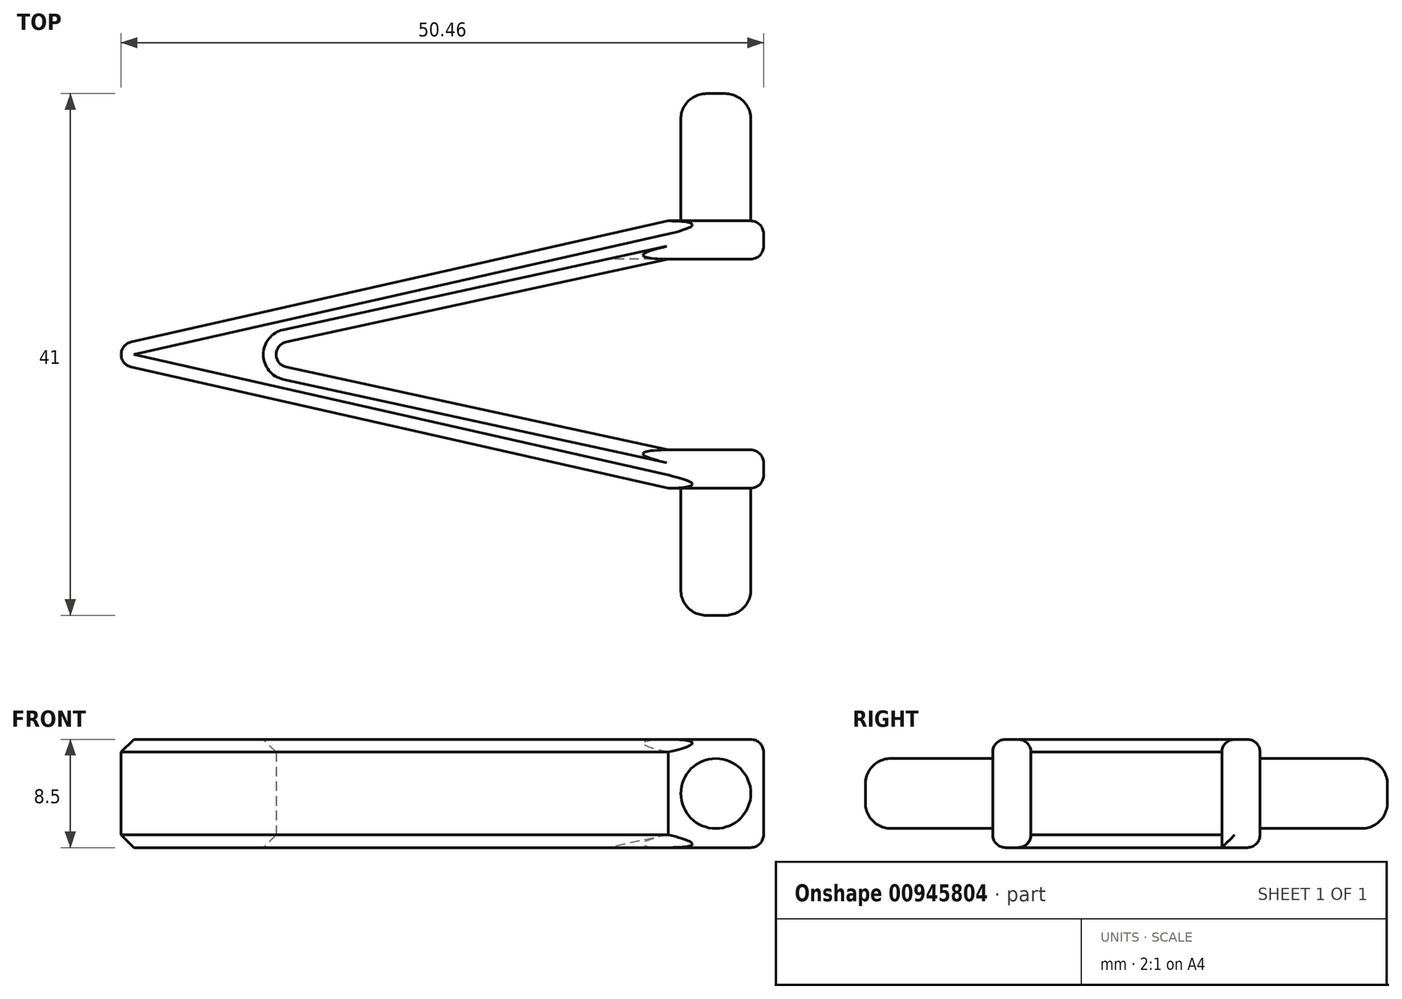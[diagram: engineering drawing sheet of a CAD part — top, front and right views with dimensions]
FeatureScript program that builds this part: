
annotation { "Feature Type Name" : "Feature", "Feature Type Description" : "" }
export const myFeature = defineFeature(function(context is Context, id is Id, definition is map)
    precondition{}
    {
        {
            var Q0;
            Q0=qCreatedBy(makeId("Top.planeOp"),FACE);
            var sketch = newSketch(context, id + "F0", { "sketchPlane" : qUnion([Q0])});
            skLineSegment(sketch, "E0", {"start": v(0, 10.5) * mm, "end": v(0, -10.5) * mm, "construction": true});
            skLineSegment(sketch, "E1", {"start": v(0, 0) * mm, "end": v(-54, 0) * mm, "construction": true});
            skPoint(sketch, "E1.endSnap0", {"position": v(0, 0) * mm});
            skLineSegment(sketch, "E2", {"start": v(0, 10.5) * mm, "end": v(-7.5, 10.5) * mm});
            skLineSegment(sketch, "E3", {"start": v(-7.5, 10.5) * mm, "end": v(-54, 0) * mm});
            skLineSegment(sketch, "E4", {"start": v(0, 10.5) * mm, "end": v(0, 7.5) * mm});
            skLineSegment(sketch, "E5", {"start": v(0, 7.5) * mm, "end": v(-7.5, 7.5) * mm});
            skLineSegment(sketch, "E6", {"start": v(-7.5, 7.5) * mm, "end": v(-42, 0) * mm});
            skLineSegment(sketch, "E7.MirrorCS", {"start": v(-7.5, -10.5) * mm, "end": v(-54, 0) * mm});
            skLineSegment(sketch, "E8.MirrorCS", {"start": v(0, -7.5) * mm, "end": v(-7.5, -7.5) * mm});
            skLineSegment(sketch, "E9.MirrorCS", {"start": v(0, -10.5) * mm, "end": v(0, -7.5) * mm});
            skLineSegment(sketch, "E10.MirrorCS", {"start": v(0, -10.5) * mm, "end": v(-7.5, -10.5) * mm});
            skLineSegment(sketch, "E11.MirrorCS", {"start": v(-7.5, -7.5) * mm, "end": v(-42, 0) * mm});
            skSolve(sketch);
        }
        {
            var Q0;
            Q0 = qSketchRegion(id + "F0", true);
            extrude(context, id + "F1", {"entities" : qUnion([Q0]), "depth" : 8.5 * mm, "offsetDistance" : 25 * mm});
        }
        {
            var Q0;
            Q0=makeQuery(id+"F1.opExtrude","SWEPT_EDGE",EDGE,{"disambiguationData":[OSD([sQuery(id+"F0.wireOp",EDGE,"E6"),sQuery(id+"F0.wireOp",EDGE,"E11.MirrorCS")])]});
            fillet(context, id + "F2", {"entities" : qUnion([Q0]), "radius" : 1 * mm, "tangentPropagation" : true, "allowEdgeOverflow" : false});
        }
        {
            var Q0;
            Q0=makeQuery(id+"F1.opExtrude","SWEPT_EDGE",EDGE,{"disambiguationData":[OSD([sQuery(id+"F0.wireOp",EDGE,"E3"),sQuery(id+"F0.wireOp",EDGE,"E7.MirrorCS")])]});
            fillet(context, id + "F3", {"entities" : qUnion([Q0]), "radius" : 1 * mm, "tangentPropagation" : true, "allowEdgeOverflow" : false});
        }
        {
            var Q0;
            Q0=makeQuery(id+"F1.opExtrude","SWEPT_FACE",FACE,{"disambiguationData":[OSD([sQuery(id+"F0.wireOp",EDGE,"E2")])]});
            var sketch = newSketch(context, id + "F4", { "sketchPlane" : qUnion([Q0])});
            skCircle(sketch, "E12", {"center": v(3.75, 4.25) * mm, "radius": 2.75 * mm});
            skLineSegment(sketch, "E13", {"start": v(7.5, 8.5) * mm, "end": v(0, 0) * mm, "construction": true});
            skLineSegment(sketch, "E14", {"start": v(0, 8.5) * mm, "end": v(7.5, 0) * mm, "construction": true});
            skSolve(sketch);
        }
        {
            var Q0;
            Q0 = qSketchRegion(id + "F4", true);
            extrude(context, id + "F5", {"entities" : qUnion([Q0]), "operationType" : NewBodyOperationType.ADD, "depth" : 10 * mm, "offsetDistance" : 25 * mm});
        }
        {
            var Q0;
            Q0=makeQuery(id+"F1.opExtrude","SWEPT_FACE",FACE,{"disambiguationData":[OSD([sQuery(id+"F0.wireOp",EDGE,"E10.MirrorCS")])]});
            var sketch = newSketch(context, id + "F6", { "sketchPlane" : qUnion([Q0])});
            skLineSegment(sketch, "E15", {"start": v(0, 8.5) * mm, "end": v(-7.5, 0) * mm, "construction": true});
            skLineSegment(sketch, "E16", {"start": v(-7.5, 8.5) * mm, "end": v(0, 0) * mm, "construction": true});
            skPoint(sketch, "E17", {"position": v(-3.75, 4.25) * mm});
            skCircle(sketch, "E18", {"center": v(-3.75, 4.25) * mm, "radius": 2.75 * mm});
            skSolve(sketch);
        }
        {
            var Q0;
            Q0 = qSketchRegion(id + "F6", true);
            extrude(context, id + "F7", {"entities" : qUnion([Q0]), "operationType" : NewBodyOperationType.ADD, "depth" : 10 * mm, "offsetDistance" : 25 * mm});
        }
        {
            var Q0;
            Q0=makeQuery(id+"F7.opExtrude","CAP_EDGE",EDGE,{"disambiguationData":[OSD([sQuery(id+"F6.wireOp",EDGE,"E18")])],"isStart":false});
            var Q1;
            Q1=makeQuery(id+"F5.opExtrude","CAP_EDGE",EDGE,{"disambiguationData":[OSD([sQuery(id+"F4.wireOp",EDGE,"E12")])],"isStart":false});
            fillet(context, id + "F8", {"entities" : qUnion([Q0, Q1]), "radius" : 2 * mm, "tangentPropagation" : true, "allowEdgeOverflow" : false});
        }
        {
            var Q0;
            Q0=makeQuery(id+"F1.opExtrude","CAP_EDGE",EDGE,{"disambiguationData":[OSD([sQuery(id+"F0.wireOp",EDGE,"E7.MirrorCS")])],"isStart":false});
            var Q1;
            Q1=makeQuery(id+"F1.opExtrude","CAP_EDGE",EDGE,{"disambiguationData":[OSD([sQuery(id+"F0.wireOp",EDGE,"E7.MirrorCS")])],"isStart":true});
            var Q2;
            Q2=makeQuery(id+"F1.opExtrude","CAP_EDGE",EDGE,{"disambiguationData":[OSD([sQuery(id+"F0.wireOp",EDGE,"E6")])],"isStart":true});
            var Q3;
            Q3=makeQuery(id+"F1.opExtrude","CAP_EDGE",EDGE,{"disambiguationData":[OSD([sQuery(id+"F0.wireOp",EDGE,"E11.MirrorCS")])],"isStart":false});
            chamfer(context, id + "F9", {"entities" : qUnion([Q0, Q1, Q2, Q3]), "width" : 1 * mm, "tangentPropagation" : true});
        }
        {
            var Q0;
            Q0=makeQuery(id+"F1.opExtrude","CAP_EDGE",EDGE,{"disambiguationData":[OSD([sQuery(id+"F0.wireOp",EDGE,"E5")])],"isStart":false});
            var Q1;
            Q1=makeQuery(id+"F1.opExtrude","CAP_EDGE",EDGE,{"disambiguationData":[OSD([sQuery(id+"F0.wireOp",EDGE,"E2")])],"isStart":false});
            var Q2;
            Q2=makeQuery(id+"F1.opExtrude","CAP_EDGE",EDGE,{"disambiguationData":[OSD([sQuery(id+"F0.wireOp",EDGE,"E4")])],"isStart":false});
            var Q3;
            Q3=makeQuery(id+"F1.opExtrude","SWEPT_EDGE",EDGE,{"disambiguationData":[OSD([sQuery(id+"F0.wireOp",EDGE,"E4"),sQuery(id+"F0.wireOp",EDGE,"E5")])]});
            var Q4;
            Q4=makeQuery(id+"F1.opExtrude","CAP_EDGE",EDGE,{"disambiguationData":[OSD([sQuery(id+"F0.wireOp",EDGE,"E4")])],"isStart":true});
            var Q5;
            Q5=makeQuery(id+"F1.opExtrude","SWEPT_EDGE",EDGE,{"disambiguationData":[OSD([sQuery(id+"F0.wireOp",EDGE,"E2"),sQuery(id+"F0.wireOp",EDGE,"E4")])]});
            var Q6;
            Q6=makeQuery(id+"F1.opExtrude","CAP_EDGE",EDGE,{"disambiguationData":[OSD([sQuery(id+"F0.wireOp",EDGE,"E2")])],"isStart":true});
            var Q7;
            Q7=makeQuery(id+"F1.opExtrude","CAP_EDGE",EDGE,{"disambiguationData":[OSD([sQuery(id+"F0.wireOp",EDGE,"E8.MirrorCS")])],"isStart":true});
            var Q8;
            Q8=makeQuery(id+"F1.opExtrude","CAP_EDGE",EDGE,{"disambiguationData":[OSD([sQuery(id+"F0.wireOp",EDGE,"E9.MirrorCS")])],"isStart":true});
            var Q9;
            Q9=makeQuery(id+"F1.opExtrude","CAP_EDGE",EDGE,{"disambiguationData":[OSD([sQuery(id+"F0.wireOp",EDGE,"E10.MirrorCS")])],"isStart":true});
            var Q10;
            Q10=makeQuery(id+"F1.opExtrude","SWEPT_EDGE",EDGE,{"disambiguationData":[OSD([sQuery(id+"F0.wireOp",EDGE,"E8.MirrorCS"),sQuery(id+"F0.wireOp",EDGE,"E9.MirrorCS")])]});
            var Q11;
            Q11=makeQuery(id+"F1.opExtrude","SWEPT_EDGE",EDGE,{"disambiguationData":[OSD([sQuery(id+"F0.wireOp",EDGE,"E9.MirrorCS"),sQuery(id+"F0.wireOp",EDGE,"E10.MirrorCS")])]});
            var Q12;
            Q12=makeQuery(id+"F1.opExtrude","CAP_EDGE",EDGE,{"disambiguationData":[OSD([sQuery(id+"F0.wireOp",EDGE,"E9.MirrorCS")])],"isStart":false});
            var Q13;
            Q13=makeQuery(id+"F1.opExtrude","CAP_EDGE",EDGE,{"disambiguationData":[OSD([sQuery(id+"F0.wireOp",EDGE,"E8.MirrorCS")])],"isStart":false});
            var Q14;
            Q14=makeQuery(id+"F1.opExtrude","CAP_EDGE",EDGE,{"disambiguationData":[OSD([sQuery(id+"F0.wireOp",EDGE,"E10.MirrorCS")])],"isStart":false});
            fillet(context, id + "F10", {"entities" : qUnion([Q0, Q1, Q2, Q3, Q4, Q5, Q6, Q7, Q8, Q9, Q10, Q11, Q12, Q13, Q14]), "radius" : 1 * mm, "tangentPropagation" : true, "allowEdgeOverflow" : false});
        }
    });
